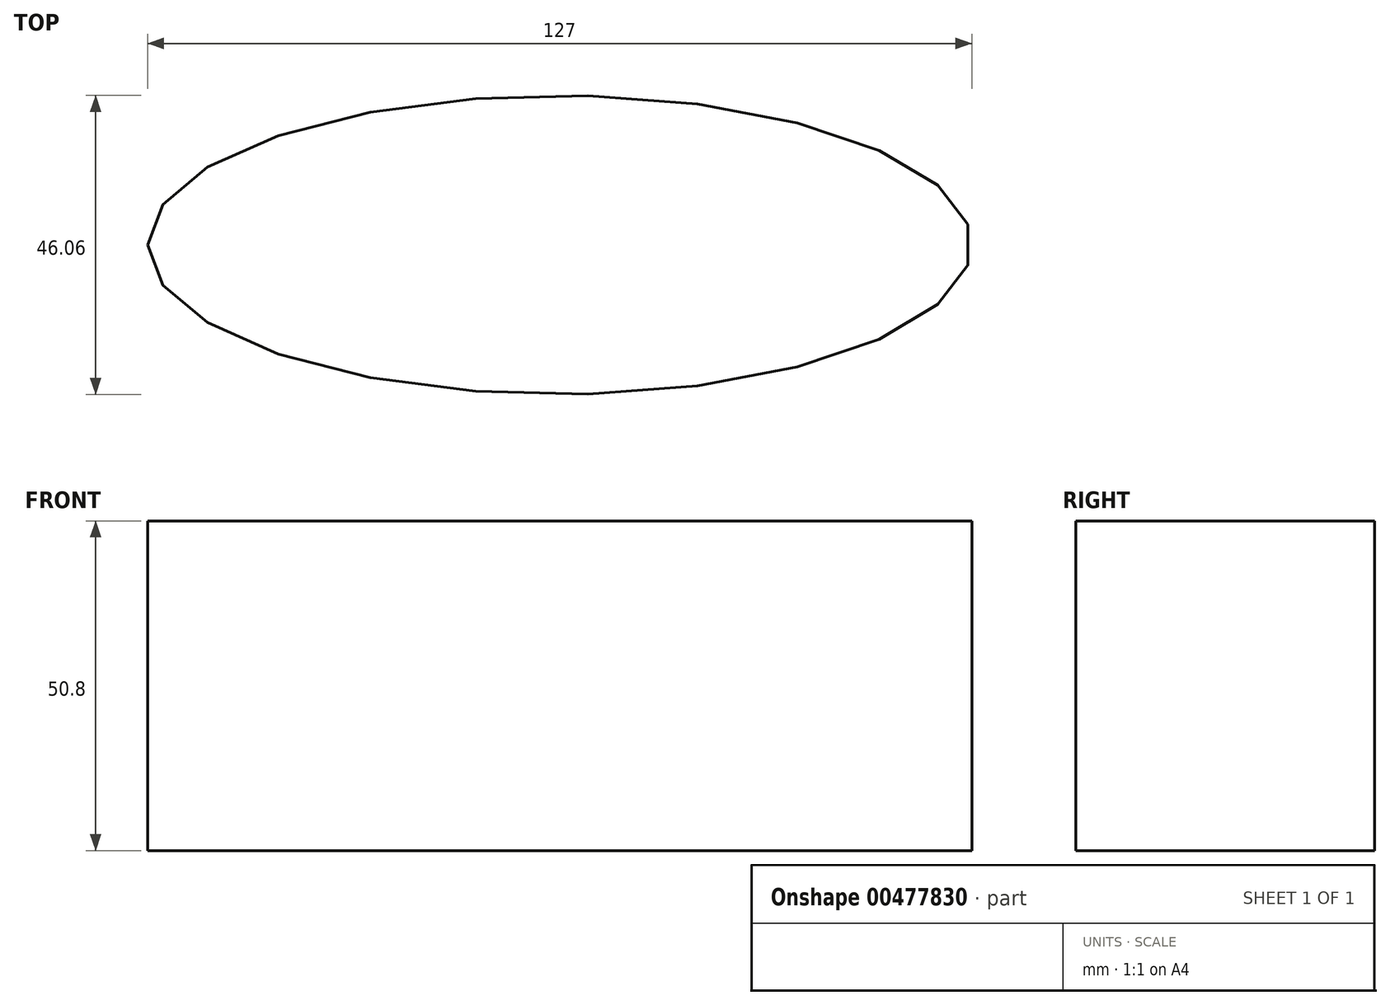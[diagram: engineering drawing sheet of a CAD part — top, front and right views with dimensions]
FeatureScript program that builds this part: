
annotation { "Feature Type Name" : "Feature", "Feature Type Description" : "" }
export const myFeature = defineFeature(function(context is Context, id is Id, definition is map)
    precondition{}
    {
        {
            var Q0;
            Q0=qCreatedBy(makeId("Top.planeOp"),FACE);
            var sketch = newSketch(context, id + "F0", { "sketchPlane" : qUnion([Q0])});
            skEllipse(sketch, "E0", {"center": v(0, 0) * mm, "majorRadius": 63.5 * mm, "minorRadius": 23.03 * mm, "majorAxis": v(-1, 0)});
            skSolve(sketch);
        }
        {
            var Q0;
            Q0=makeQuery(id+"F0.imprint","IMPRINT",FACE,{"disambiguationData":[TD([[makeQuery(id+"F0.imprint","IMPRINT",EDGE,{"derivedFrom":sQuery(id+"F0.wireOp",EDGE,"E0")}),1.0]])]});
            extrude(context, id + "F1", {"entities" : qUnion([Q0]), "depth" : 50.8 * mm});
        }
    });
